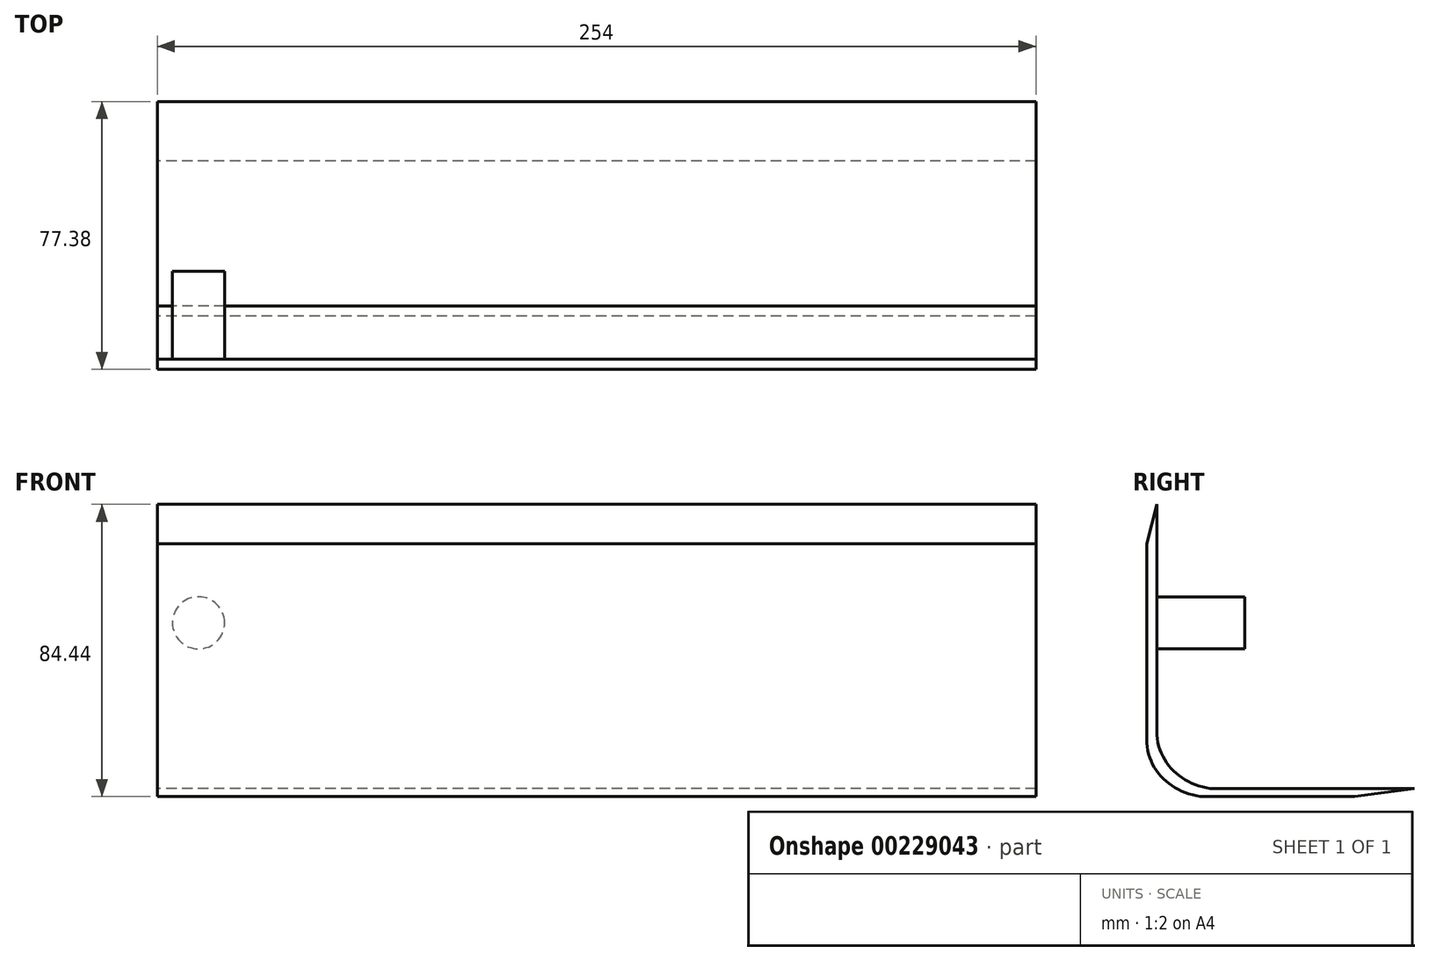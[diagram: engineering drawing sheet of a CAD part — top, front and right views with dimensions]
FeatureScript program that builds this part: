
annotation { "Feature Type Name" : "Feature", "Feature Type Description" : "" }
export const myFeature = defineFeature(function(context is Context, id is Id, definition is map)
    precondition{}
    {
        {
            var Q0;
            Q0=qCreatedBy(makeId("Right.planeOp"),FACE);
            var sketch = newSketch(context, id + "F0", { "sketchPlane" : qUnion([Q0])});
            skLineSegment(sketch, "E0", {"start": v(0, 56.34) * mm, "end": v(0, 0) * mm});
            skLineSegment(sketch, "E1", {"start": v(15.4, -16.69) * mm, "end": v(60.19, -16.69) * mm});
            skFitSpline(sketch, "E2", {"points": [v(0, 0) * mm, v(15.4, -16.69) * mm], "startDerivative": vector(0, -26.96) * mm, "endDerivative": vector(25.67, -4.28) * mm});
            skLineSegment(sketch, "E3", {"start": v(2.94, 67.75) * mm, "end": v(2.94, 2.29) * mm});
            skLineSegment(sketch, "E4", {"start": v(18.34, -14.4) * mm, "end": v(77.38, -14.4) * mm});
            skFitSpline(sketch, "E5", {"points": [v(2.94, 2.29) * mm, v(18.34, -14.4) * mm], "startDerivative": vector(0, -26.96) * mm, "endDerivative": vector(25.67, -4.28) * mm});
            skLineSegment(sketch, "E6", {"start": v(2.94, 67.75) * mm, "end": v(0, 56.34) * mm});
            skLineSegment(sketch, "E7", {"start": v(60.19, -16.69) * mm, "end": v(77.38, -14.4) * mm});
            skSolve(sketch);
        }
        {
            var Q0;
            Q0=makeQuery(id+"F0.imprint","IMPRINT",FACE,{"disambiguationData":[TD([[makeQuery(id+"F0.imprint","IMPRINT",EDGE,{"derivedFrom":sQuery(id+"F0.wireOp",EDGE,"E0")}),1.0]])]});
            extrude(context, id + "F1", {"entities" : qUnion([Q0]), "depth" : 254 * mm});
        }
        {
            var Q0;
            Q0=makeQuery(id+"F1.opExtrude","SWEPT_FACE",FACE,{"disambiguationData":[OSD([sQuery(id+"F0.wireOp",EDGE,"E3")])]});
            var sketch = newSketch(context, id + "F2", { "sketchPlane" : qUnion([Q0])});
            skCircle(sketch, "E8", {"center": v(-11.93, 33.52) * mm, "radius": 7.54 * mm});
            skSolve(sketch);
        }
        {
            var Q0;
            Q0=makeQuery(id+"F2.imprint","IMPRINT",FACE,{"disambiguationData":[TD([[makeQuery(id+"F2.imprint","IMPRINT",EDGE,{"derivedFrom":sQuery(id+"F2.wireOp",EDGE,"E8")}),1.0]])]});
            extrude(context, id + "F3", {"entities" : qUnion([Q0]), "operationType" : NewBodyOperationType.ADD, "depth" : 25.4 * mm});
        }
        {
            var Q0;
            Q0=sQuery(id+"F2.wireOp",EDGE,"E8");
            extrude(context, id + "F4", {"bodyType" : ToolBodyType.SURFACE, "surfaceEntities" : qUnion([Q0]), "depth" : 25.4 * mm});
        }
    });
